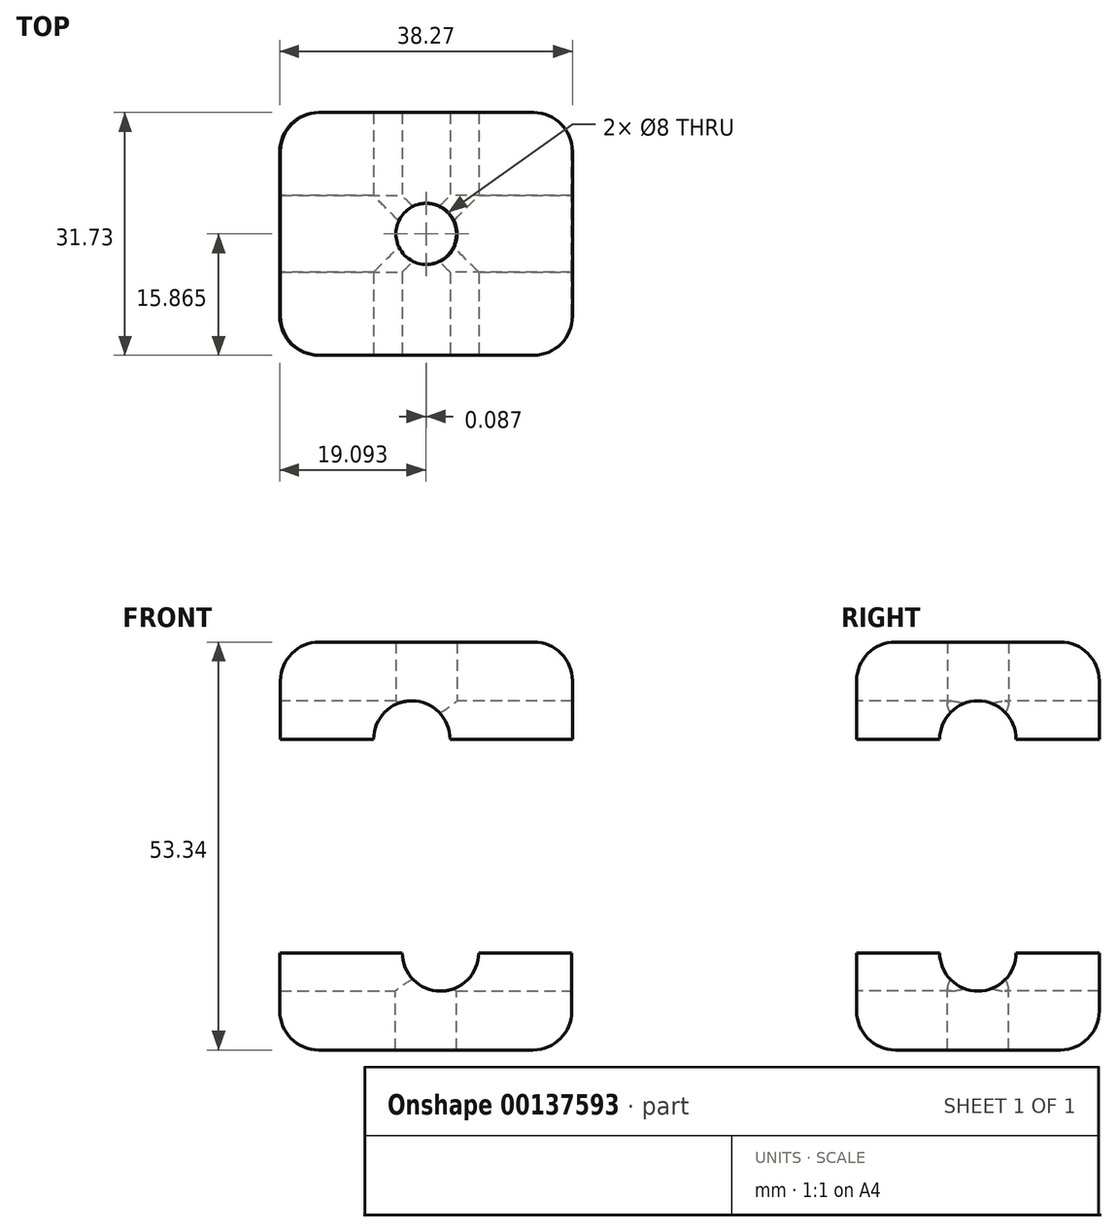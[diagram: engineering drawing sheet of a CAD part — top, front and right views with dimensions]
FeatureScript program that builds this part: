
annotation { "Feature Type Name" : "Feature", "Feature Type Description" : "" }
export const myFeature = defineFeature(function(context is Context, id is Id, definition is map)
    precondition{}
    {
        {
            var Q0;
            Q0=qCreatedBy(makeId("Top.planeOp"),FACE);
            var sketch = newSketch(context, id + "F0", { "sketchPlane" : qUnion([Q0])});
            skLineSegment(sketch, "E0.bottom", {"start": v(-17.17, 17.38) * mm, "end": v(21.01, 17.38) * mm});
            skLineSegment(sketch, "E0.top", {"start": v(-17.17, -14.35) * mm, "end": v(21.01, -14.35) * mm});
            skLineSegment(sketch, "E0.left", {"start": v(-17.17, 17.38) * mm, "end": v(-17.17, -14.35) * mm});
            skLineSegment(sketch, "E0.right", {"start": v(21.01, 17.38) * mm, "end": v(21.01, -14.35) * mm});
            skSolve(sketch);
        }
        {
            var Q0;
            Q0 = qSketchRegion(id + "F0", true);
            extrude(context, id + "F1", {"entities" : qUnion([Q0]), "depth" : 25.4 * mm});
        }
        {
            var Q0;
            Q0=makeQuery(id+"F1.opExtrude","CAP_FACE",FACE,{"disambiguationData":[OSD([sQuery(id+"F0.wireOp",EDGE,"E0.bottom"),sQuery(id+"F0.wireOp",EDGE,"E0.top"),sQuery(id+"F0.wireOp",EDGE,"E0.left"),sQuery(id+"F0.wireOp",EDGE,"E0.right")])],"isStart":true});
            var sketch = newSketch(context, id + "F2", { "sketchPlane" : qUnion([Q0])});
            skCircle(sketch, "E1", {"center": v(1.92, -1.52) * mm, "radius": 4 * mm});
            skPoint(sketch, "E1.centerSnap0", {"position": v(1.92, -17.38) * mm});
            skPoint(sketch, "E1.centerSnap1", {"position": v(-17.17, -1.52) * mm});
            skSolve(sketch);
        }
        {
            var Q0;
            Q0=makeQuery(id+"F2.imprint","IMPRINT",FACE,{"disambiguationData":[TD([[makeQuery(id+"F2.imprint","IMPRINT",EDGE,{"derivedFrom":sQuery(id+"F2.wireOp",EDGE,"E1")}),1.0]])]});
            extrude(context, id + "F3", {"entities" : qUnion([Q0]), "operationType" : NewBodyOperationType.REMOVE, "endBound" : BoundingType.THROUGH_ALL, "oppositeDirection" : true, "depth" : 25.4 * mm});
        }
        {
            var Q0;
            Q0=makeQuery(id+"F1.opExtrude","CAP_EDGE",EDGE,{"disambiguationData":[OSD([sQuery(id+"F0.wireOp",EDGE,"E0.top")])],"isStart":false});
            var Q1;
            Q1=makeQuery(id+"F1.opExtrude","SWEPT_EDGE",EDGE,{"disambiguationData":[OSD([sQuery(id+"F0.wireOp",EDGE,"E0.top"),sQuery(id+"F0.wireOp",EDGE,"E0.right")])]});
            var Q2;
            Q2=makeQuery(id+"F1.opExtrude","SWEPT_EDGE",EDGE,{"disambiguationData":[OSD([sQuery(id+"F0.wireOp",EDGE,"E0.bottom"),sQuery(id+"F0.wireOp",EDGE,"E0.right")])]});
            var Q3;
            Q3=makeQuery(id+"F1.opExtrude","CAP_EDGE",EDGE,{"disambiguationData":[OSD([sQuery(id+"F0.wireOp",EDGE,"E0.right")])],"isStart":false});
            var Q4;
            Q4=makeQuery(id+"F1.opExtrude","CAP_EDGE",EDGE,{"disambiguationData":[OSD([sQuery(id+"F0.wireOp",EDGE,"E0.left")])],"isStart":false});
            var Q5;
            Q5=makeQuery(id+"F1.opExtrude","CAP_EDGE",EDGE,{"disambiguationData":[OSD([sQuery(id+"F0.wireOp",EDGE,"E0.right")])],"isStart":true});
            var Q6;
            Q6=makeQuery(id+"F1.opExtrude","CAP_EDGE",EDGE,{"disambiguationData":[OSD([sQuery(id+"F0.wireOp",EDGE,"E0.left")])],"isStart":true});
            var Q7;
            Q7=makeQuery(id+"F1.opExtrude","CAP_EDGE",EDGE,{"disambiguationData":[OSD([sQuery(id+"F0.wireOp",EDGE,"E0.top")])],"isStart":true});
            var Q8;
            Q8=makeQuery(id+"F1.opExtrude","CAP_EDGE",EDGE,{"disambiguationData":[OSD([sQuery(id+"F0.wireOp",EDGE,"E0.bottom")])],"isStart":false});
            var Q9;
            Q9=makeQuery(id+"F1.opExtrude","CAP_EDGE",EDGE,{"disambiguationData":[OSD([sQuery(id+"F0.wireOp",EDGE,"E0.bottom")])],"isStart":true});
            var Q10;
            Q10=makeQuery(id+"F1.opExtrude","SWEPT_EDGE",EDGE,{"disambiguationData":[OSD([sQuery(id+"F0.wireOp",EDGE,"E0.top"),sQuery(id+"F0.wireOp",EDGE,"E0.left")])]});
            var Q11;
            Q11=makeQuery(id+"F1.opExtrude","SWEPT_EDGE",EDGE,{"disambiguationData":[OSD([sQuery(id+"F0.wireOp",EDGE,"E0.bottom"),sQuery(id+"F0.wireOp",EDGE,"E0.left")])]});
            fillet(context, id + "F4", {"entities" : qUnion([Q0, Q1, Q2, Q3, Q4, Q5, Q6, Q7, Q8, Q9, Q10, Q11]), "radius" : 5.08 * mm, "tangentPropagation" : true, "allowEdgeOverflow" : false});
        }
        {
            var Q0;
            Q0=makeQuery(id+"F1.opExtrude","SWEPT_FACE",FACE,{"disambiguationData":[OSD([sQuery(id+"F0.wireOp",EDGE,"E0.left")])]});
            var sketch = newSketch(context, id + "F5", { "sketchPlane" : qUnion([Q0])});
            skCircle(sketch, "E2", {"center": v(-1.52, 12.7) * mm, "radius": 5 * mm});
            skPoint(sketch, "E2.centerSnap0", {"position": v(-1.52, 20.32) * mm});
            skPoint(sketch, "E2.centerSnap1", {"position": v(-12.3, 12.7) * mm});
            skSolve(sketch);
        }
        {
            var Q0;
            Q0=makeQuery(id+"F5.imprint","IMPRINT",FACE,{"disambiguationData":[TD([[makeQuery(id+"F5.imprint","IMPRINT",EDGE,{"derivedFrom":sQuery(id+"F5.wireOp",EDGE,"E2")}),1.0]])]});
            extrude(context, id + "F6", {"entities" : qUnion([Q0]), "operationType" : NewBodyOperationType.REMOVE, "endBound" : BoundingType.THROUGH_ALL, "oppositeDirection" : true, "depth" : 25.4 * mm});
        }
        {
            var Q0;
            Q0=makeQuery(id+"F1.opExtrude","SWEPT_FACE",FACE,{"disambiguationData":[OSD([sQuery(id+"F0.wireOp",EDGE,"E0.top")])]});
            var sketch = newSketch(context, id + "F7", { "sketchPlane" : qUnion([Q0])});
            skCircle(sketch, "E3", {"center": v(0, 12.7) * mm, "radius": 5 * mm});
            skPoint(sketch, "E3.centerSnap0", {"position": v(-12.1, 12.7) * mm});
            skSolve(sketch);
        }
        {
            var Q0;
            Q0=makeQuery(id+"F7.imprint","IMPRINT",FACE,{"disambiguationData":[TD([[makeQuery(id+"F7.imprint","IMPRINT",EDGE,{"derivedFrom":sQuery(id+"F7.wireOp",EDGE,"E3")}),1.0]])]});
            extrude(context, id + "F8", {"entities" : qUnion([Q0]), "operationType" : NewBodyOperationType.REMOVE, "endBound" : BoundingType.THROUGH_ALL, "oppositeDirection" : true, "depth" : 25.4 * mm});
        }
        {
            var Q0;
            Q0=makeQuery(id+"F1.opExtrude","SWEPT_FACE",FACE,{"disambiguationData":[OSD([sQuery(id+"F0.wireOp",EDGE,"E0.left")])]});
            var sketch = newSketch(context, id + "F9", { "sketchPlane" : qUnion([Q0])});
            skLineSegment(sketch, "E4", {"start": v(-1.52, 12.7) * mm, "end": v(24.54, 12.7) * mm, "construction": true});
            skPoint(sketch, "E4.endSnap0", {"position": v(9.27, 12.7) * mm});
            skLineSegment(sketch, "E5.bottom", {"start": v(24.54, 12.7) * mm, "end": v(-48.54, 12.7) * mm});
            skLineSegment(sketch, "E5.top", {"start": v(24.54, -21.73) * mm, "end": v(-48.54, -21.73) * mm});
            skLineSegment(sketch, "E5.left", {"start": v(24.54, 12.7) * mm, "end": v(24.54, -21.73) * mm});
            skLineSegment(sketch, "E5.right", {"start": v(-48.54, 12.7) * mm, "end": v(-48.54, -21.73) * mm});
            skSolve(sketch);
        }
        {
            var Q0;
            Q0=makeQuery(id+"F9.imprint","IMPRINT",FACE,{"disambiguationData":[TD([[makeQuery(id+"F9.imprint","IMPRINT",EDGE,{"derivedFrom":sQuery(id+"F9.wireOp",EDGE,"E5.top")}),-1.0]])]});
            var Q1;
            {var subQ0=sQuery(id+"F0.wireOp",EDGE,"E0.left");var subQ1=makeQuery(id+"F1.opExtrude","SWEPT_FACE",FACE,{"disambiguationData":[OSD([subQ0])]});var subQ2=makeQuery(id+"F4.opFillet","BLEND_EDGE",EDGE,{"blendedFrom":[makeQuery(id+"F1.opExtrude","CAP_EDGE",EDGE,{"disambiguationData":[OSD([subQ0])],"isStart":true}),subQ1],"blendedInto":[subQ1]});Q1=makeQuery(id+"F9.imprint","IMPRINT",FACE,{"disambiguationData":[TD([[makeQuery(id+"F9.imprint","IMPRINT",EDGE,{"derivedFrom":subQ2}),1.0]])]});}
            var Q2;
            {var subQ0=sQuery(id+"F9.wireOp",EDGE,"E5.bottom");var subQ1=makeQuery(id+"F6.boolean.opBoolean","COPY",EDGE,{"derivedFrom":makeQuery(id+"F6.opExtrude","CAP_EDGE",EDGE,{"disambiguationData":[OSD([sQuery(id+"F5.wireOp",EDGE,"E2")])],"isStart":true})});var subQ2=makeQuery(id+"F9.imprint","INTERSECT",VERTEX,{"disambiguationData":[OD(0.0)],"derivedFrom":[subQ1,subQ0]});Q2=makeQuery(id+"F9.imprint","IMPRINT",FACE,{"disambiguationData":[TD([[makeQuery(id+"F9.imprint","IMPRINT",EDGE,{"disambiguationData":[TD([[subQ2,-1.0]])],"derivedFrom":subQ0}),1.0]])]});}
            extrude(context, id + "F10", {"entities" : qUnion([Q0, Q1, Q2]), "operationType" : NewBodyOperationType.REMOVE, "endBound" : BoundingType.THROUGH_ALL, "oppositeDirection" : true, "depth" : 25.4 * mm});
        }
        {
            var Q0;
            Q0=makeQuery(id+"F1.opExtrude","SWEPT_BODY",BODY,{"disambiguationData":[OSD([sQuery(id+"F0.wireOp",EDGE,"E0.bottom"),sQuery(id+"F0.wireOp",EDGE,"E0.top"),sQuery(id+"F0.wireOp",EDGE,"E0.left"),sQuery(id+"F0.wireOp",EDGE,"E0.right")])]});
            transform(context, id + "F11", {"entities" : qUnion([Q0]), "transformType" : TransformType.TRANSLATION_3D, "dx" : 101.6 * mm, "dy" : 101.6 * mm, "dz" : 101.6 * mm, "makeCopy" : true});
        }
        {
            var Q0;
            Q0=makeQuery(id+"F11.opPattern","COPY",BODY,{"derivedFrom":makeQuery(id+"F1.opExtrude","SWEPT_BODY",BODY,{"disambiguationData":[OSD([sQuery(id+"F0.wireOp",EDGE,"E0.bottom"),sQuery(id+"F0.wireOp",EDGE,"E0.top"),sQuery(id+"F0.wireOp",EDGE,"E0.left"),sQuery(id+"F0.wireOp",EDGE,"E0.right")])]}),"instanceName":"1"});
            transform(context, id + "F12", {"entities" : qUnion([Q0]), "transformType" : TransformType.TRANSLATION_3D, "dx" : 0 * mm, "dy" : 0 * mm, "dz" : 0 * mm, "makeCopy" : true});
        }
        {
            var Q0;
            Q0=makeQuery(id+"F12.opPattern","COPY",BODY,{"derivedFrom":makeQuery(id+"F11.opPattern","COPY",BODY,{"derivedFrom":makeQuery(id+"F1.opExtrude","SWEPT_BODY",BODY,{"disambiguationData":[OSD([sQuery(id+"F0.wireOp",EDGE,"E0.bottom"),sQuery(id+"F0.wireOp",EDGE,"E0.top"),sQuery(id+"F0.wireOp",EDGE,"E0.left"),sQuery(id+"F0.wireOp",EDGE,"E0.right")])]}),"instanceName":"1"}),"instanceName":"1"});
            deleteBodies(context, id + "F13", {"entities" : qUnion([Q0])});
        }
        {
            var Q0;
            Q0=makeQuery(id+"F11.opPattern","COPY",BODY,{"derivedFrom":makeQuery(id+"F1.opExtrude","SWEPT_BODY",BODY,{"disambiguationData":[OSD([sQuery(id+"F0.wireOp",EDGE,"E0.bottom"),sQuery(id+"F0.wireOp",EDGE,"E0.top"),sQuery(id+"F0.wireOp",EDGE,"E0.left"),sQuery(id+"F0.wireOp",EDGE,"E0.right")])]}),"instanceName":"1"});
            transform(context, id + "F14", {"entities" : qUnion([Q0]), "transformType" : TransformType.COPY});
        }
        {
            var Q0;
            Q0=makeQuery(id+"F11.opPattern","COPY",BODY,{"derivedFrom":makeQuery(id+"F1.opExtrude","SWEPT_BODY",BODY,{"disambiguationData":[OSD([sQuery(id+"F0.wireOp",EDGE,"E0.bottom"),sQuery(id+"F0.wireOp",EDGE,"E0.top"),sQuery(id+"F0.wireOp",EDGE,"E0.left"),sQuery(id+"F0.wireOp",EDGE,"E0.right")])]}),"instanceName":"1"});
            transform(context, id + "F15", {"entities" : qUnion([Q0]), "transformType" : TransformType.TRANSLATION_3D, "dx" : -99.06 * mm, "dy" : -104.14 * mm, "dz" : -154.94 * mm, "makeCopy" : false});
        }
        {
            var Q0;
            Q0=makeQuery(id+"F14.opPattern","COPY",BODY,{"derivedFrom":makeQuery(id+"F11.opPattern","COPY",BODY,{"derivedFrom":makeQuery(id+"F1.opExtrude","SWEPT_BODY",BODY,{"disambiguationData":[OSD([sQuery(id+"F0.wireOp",EDGE,"E0.bottom"),sQuery(id+"F0.wireOp",EDGE,"E0.top"),sQuery(id+"F0.wireOp",EDGE,"E0.left"),sQuery(id+"F0.wireOp",EDGE,"E0.right")])]}),"instanceName":"1"}),"instanceName":"1"});
            deleteBodies(context, id + "F16", {"entities" : qUnion([Q0])});
        }
        {
            var Q0;
            Q0=makeQuery(id+"F11.opPattern","COPY",BODY,{"derivedFrom":makeQuery(id+"F1.opExtrude","SWEPT_BODY",BODY,{"disambiguationData":[OSD([sQuery(id+"F0.wireOp",EDGE,"E0.bottom"),sQuery(id+"F0.wireOp",EDGE,"E0.top"),sQuery(id+"F0.wireOp",EDGE,"E0.left"),sQuery(id+"F0.wireOp",EDGE,"E0.right")])]}),"instanceName":"1"});
            var Q1;
            {var subQ0=sQuery(id+"F0.wireOp",EDGE,"E0.left");Q1=makeQuery(id+"F11.opPattern","COPY",EDGE,{"derivedFrom":makeQuery(id+"F4.opFillet","BLEND_EDGE",EDGE,{"blendedFrom":[makeQuery(id+"F1.opExtrude","CAP_EDGE",EDGE,{"disambiguationData":[OSD([subQ0])],"isStart":false}),makeQuery(id+"F1.opExtrude","CAP_FACE",FACE,{"disambiguationData":[OSD([sQuery(id+"F0.wireOp",EDGE,"E0.bottom"),sQuery(id+"F0.wireOp",EDGE,"E0.top"),subQ0,sQuery(id+"F0.wireOp",EDGE,"E0.right")])],"isStart":false})],"blendedInto":[makeQuery(id+"F1.opExtrude","CAP_FACE",FACE,{"disambiguationData":[OSD([sQuery(id+"F0.wireOp",EDGE,"E0.bottom"),sQuery(id+"F0.wireOp",EDGE,"E0.top"),subQ0,sQuery(id+"F0.wireOp",EDGE,"E0.right")])],"isStart":false})]}),"instanceName":"1"});}
            transform(context, id + "F17", {"entities" : qUnion([Q0]), "transformType" : TransformType.ROTATION, "transformAxis" : qUnion([Q1]), "angle" : 180 * degree, "makeCopy" : false});
        }
        {
            var Q0;
            Q0=makeQuery(id+"F11.opPattern","COPY",BODY,{"derivedFrom":makeQuery(id+"F1.opExtrude","SWEPT_BODY",BODY,{"disambiguationData":[OSD([sQuery(id+"F0.wireOp",EDGE,"E0.bottom"),sQuery(id+"F0.wireOp",EDGE,"E0.top"),sQuery(id+"F0.wireOp",EDGE,"E0.left"),sQuery(id+"F0.wireOp",EDGE,"E0.right")])]}),"instanceName":"1"});
            transform(context, id + "F18", {"entities" : qUnion([Q0]), "transformType" : TransformType.TRANSLATION_3D, "dx" : 25.4 * mm, "dy" : 2.54 * mm, "dz" : 0 * mm, "makeCopy" : false});
        }
    });
